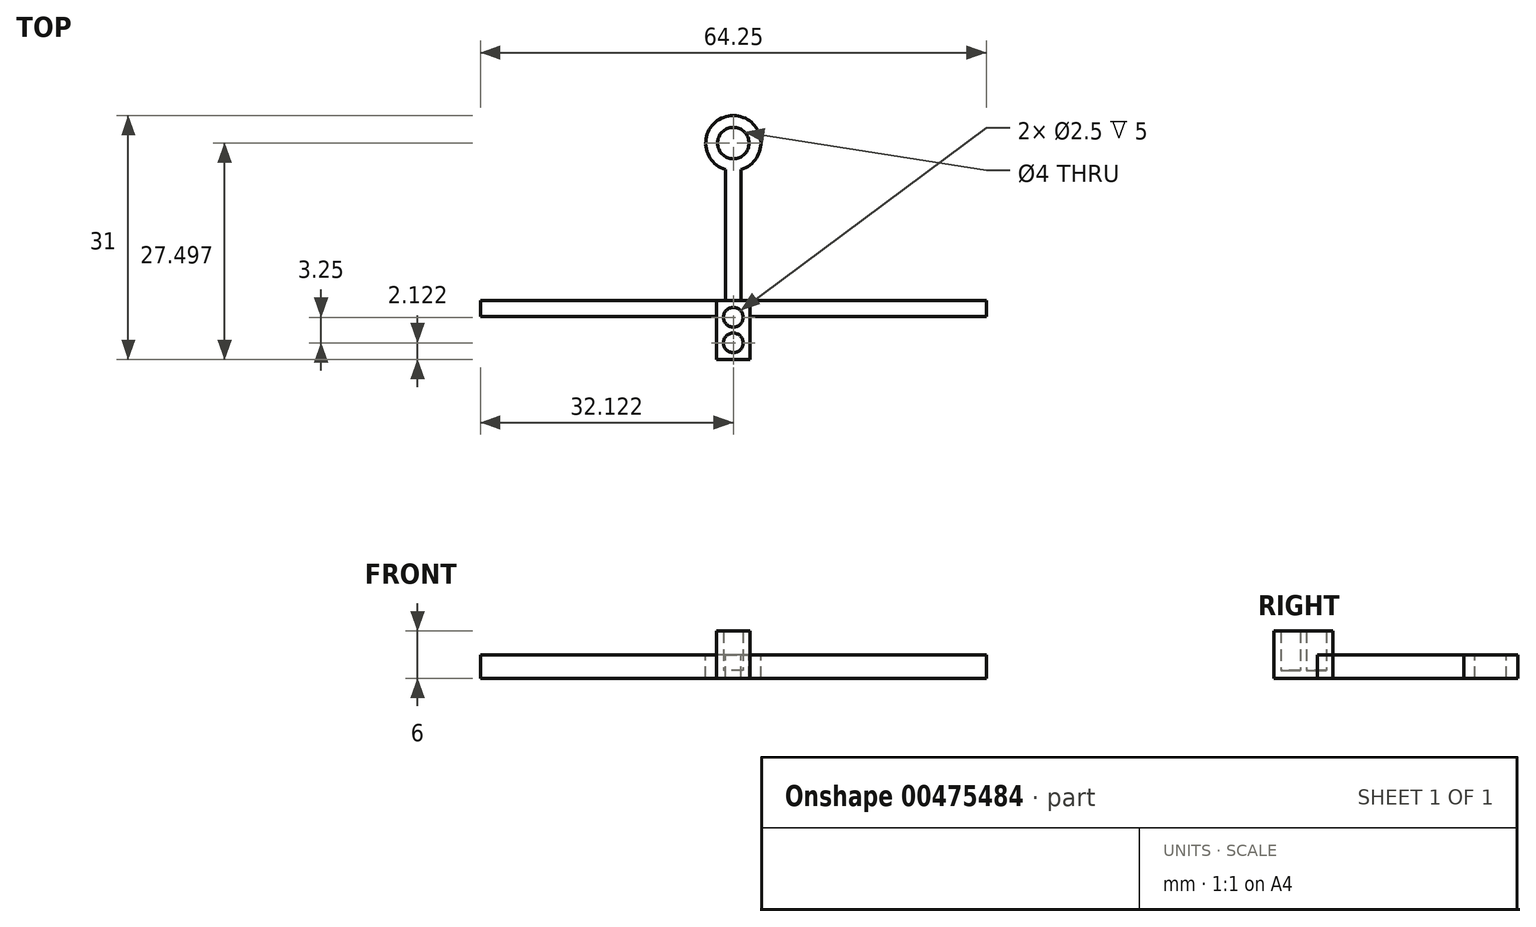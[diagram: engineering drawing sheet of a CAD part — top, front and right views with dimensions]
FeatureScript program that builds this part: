
annotation { "Feature Type Name" : "Feature", "Feature Type Description" : "" }
export const myFeature = defineFeature(function(context is Context, id is Id, definition is map)
    precondition{}
    {
        {
            var Q0;
            Q0=qCreatedBy(makeId("Top.planeOp"),FACE);
            var sketch = newSketch(context, id + "F0", { "sketchPlane" : qUnion([Q0])});
            skPoint(sketch, "E0", {"position": v(-4.95, -11.75) * mm});
            skCircle(sketch, "E1", {"center": v(-4.95, -11.75) * mm, "radius": 1.25 * mm});
            skCircle(sketch, "E2", {"center": v(-4.95, -8.5) * mm, "radius": 1.25 * mm});
            skLineSegment(sketch, "E3.bottom", {"start": v(-7.07, -6.37) * mm, "end": v(-2.82, -6.37) * mm});
            skLineSegment(sketch, "E3.top", {"start": v(-7.07, -13.87) * mm, "end": v(-2.82, -13.87) * mm});
            skLineSegment(sketch, "E3.left", {"start": v(-7.07, -6.37) * mm, "end": v(-7.07, -13.87) * mm});
            skLineSegment(sketch, "E3.right", {"start": v(-2.82, -6.37) * mm, "end": v(-2.82, -13.87) * mm});
            skCircle(sketch, "E4", {"center": v(-4.95, 13.63) * mm, "radius": 3.5 * mm});
            skPoint(sketch, "E4.centerSnap0", {"position": v(-4.95, -6.37) * mm});
            skCircle(sketch, "E5", {"center": v(-4.95, 13.63) * mm, "radius": 2 * mm});
            skLineSegment(sketch, "E6", {"start": v(-5.95, -6.37) * mm, "end": v(-5.95, 11.9) * mm});
            skLineSegment(sketch, "E7", {"start": v(-3.95, 11.9) * mm, "end": v(-3.95, -6.37) * mm});
            skLineSegment(sketch, "E8.bottom", {"start": v(-37.07, -6.37) * mm, "end": v(-7.07, -6.37) * mm});
            skLineSegment(sketch, "E8.top", {"start": v(-37.07, -8.37) * mm, "end": v(-7.07, -8.37) * mm});
            skLineSegment(sketch, "E8.left", {"start": v(-37.07, -6.37) * mm, "end": v(-37.07, -8.37) * mm});
            skLineSegment(sketch, "E8.right", {"start": v(-7.07, -6.37) * mm, "end": v(-7.07, -8.37) * mm});
            skLineSegment(sketch, "E9.bottom", {"start": v(-2.82, -6.37) * mm, "end": v(27.18, -6.37) * mm});
            skLineSegment(sketch, "E9.top", {"start": v(-2.82, -8.37) * mm, "end": v(27.18, -8.37) * mm});
            skLineSegment(sketch, "E9.left", {"start": v(-2.82, -6.37) * mm, "end": v(-2.82, -8.37) * mm});
            skLineSegment(sketch, "E9.right", {"start": v(27.18, -6.37) * mm, "end": v(27.18, -8.37) * mm});
            skSolve(sketch);
        }
        {
            var Q0;
            Q0=makeQuery(id+"F0.imprint","IMPRINT",FACE,{"disambiguationData":[TD([[makeQuery(id+"F0.imprint","IMPRINT",EDGE,{"derivedFrom":sQuery(id+"F0.wireOp",EDGE,"E1")}),-1.0]])]});
            var Q1;
            Q1=makeQuery(id+"F0.imprint","IMPRINT",FACE,{"disambiguationData":[TD([[makeQuery(id+"F0.imprint","IMPRINT",EDGE,{"derivedFrom":sQuery(id+"F0.wireOp",EDGE,"E8.bottom")}),-1.0]])]});
            var Q2;
            {var subQ0=sQuery(id+"F0.wireOp",EDGE,"E6");Q2=makeQuery(id+"F0.imprint","IMPRINT",FACE,{"disambiguationData":[TD([[makeQuery(id+"F0.imprint","IMPRINT",EDGE,{"derivedFrom":subQ0}),-1.0]])]});}
            var Q3;
            Q3=makeQuery(id+"F0.imprint","IMPRINT",FACE,{"disambiguationData":[TD([[makeQuery(id+"F0.imprint","IMPRINT",EDGE,{"derivedFrom":sQuery(id+"F0.wireOp",EDGE,"E4")}),-1.0]])]});
            var Q4;
            Q4=makeQuery(id+"F0.imprint","IMPRINT",FACE,{"disambiguationData":[TD([[makeQuery(id+"F0.imprint","IMPRINT",EDGE,{"derivedFrom":sQuery(id+"F0.wireOp",EDGE,"E9.bottom")}),-1.0]])]});
            var Q5;
            {var subQ0=sQuery(id+"F0.wireOp",EDGE,"E6");var subQ1=sQuery(id+"F0.wireOp",EDGE,"E4");var subQ2=makeQuery(id+"F0.imprint","INTERSECT",VERTEX,{"derivedFrom":[subQ1,subQ0]});Q5=makeQuery(id+"F0.imprint","IMPRINT",FACE,{"disambiguationData":[TD([[makeQuery(id+"F0.imprint","IMPRINT",EDGE,{"disambiguationData":[TD([[subQ2,1.0]])],"derivedFrom":subQ1}),1.0]])]});}
            var Q6;
            Q6=makeQuery(id+"F0.imprint","IMPRINT",FACE,{"disambiguationData":[TD([[makeQuery(id+"F0.imprint","IMPRINT",EDGE,{"derivedFrom":sQuery(id+"F0.wireOp",EDGE,"E2")}),1.0]])]});
            var Q7;
            Q7=makeQuery(id+"F0.imprint","IMPRINT",FACE,{"disambiguationData":[TD([[makeQuery(id+"F0.imprint","IMPRINT",EDGE,{"derivedFrom":sQuery(id+"F0.wireOp",EDGE,"E1")}),1.0]])]});
            extrude(context, id + "F1", {"entities" : qUnion([Q0, Q1, Q2, Q3, Q4, Q5, Q6, Q7]), "oppositeDirection" : true, "depth" : 3 * mm, "offsetDistance" : 25 * mm});
        }
        {
            var Q0;
            Q0=makeQuery(id+"F0.imprint","IMPRINT",FACE,{"disambiguationData":[TD([[makeQuery(id+"F0.imprint","IMPRINT",EDGE,{"derivedFrom":sQuery(id+"F0.wireOp",EDGE,"E1")}),-1.0]])]});
            extrude(context, id + "F2", {"entities" : qUnion([Q0]), "operationType" : NewBodyOperationType.ADD, "depth" : 3 * mm, "offsetDistance" : 25 * mm});
        }
        {
            var Q0;
            Q0=makeQuery(id+"F0.imprint","IMPRINT",FACE,{"disambiguationData":[TD([[makeQuery(id+"F0.imprint","IMPRINT",EDGE,{"derivedFrom":sQuery(id+"F0.wireOp",EDGE,"E2")}),1.0]])]});
            var Q1;
            Q1=makeQuery(id+"F0.imprint","IMPRINT",FACE,{"disambiguationData":[TD([[makeQuery(id+"F0.imprint","IMPRINT",EDGE,{"derivedFrom":sQuery(id+"F0.wireOp",EDGE,"E1")}),1.0]])]});
            extrude(context, id + "F3", {"entities" : qUnion([Q0, Q1]), "operationType" : NewBodyOperationType.REMOVE, "oppositeDirection" : true, "depth" : 2 * mm, "offsetDistance" : 25 * mm});
        }
    });
